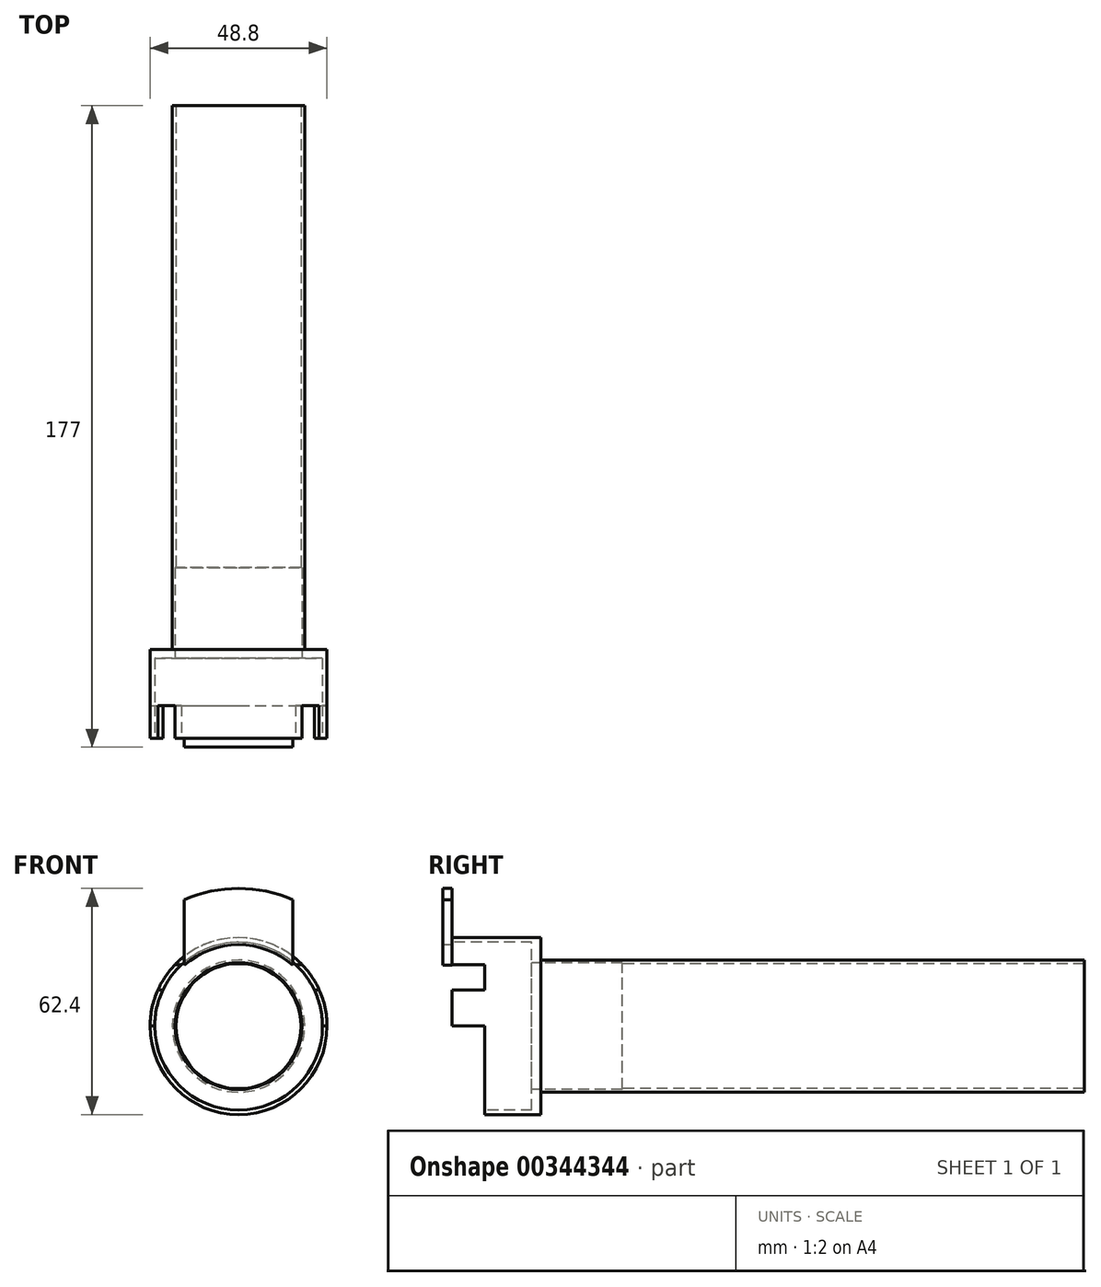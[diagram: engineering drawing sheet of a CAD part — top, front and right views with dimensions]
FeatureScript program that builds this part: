
annotation { "Feature Type Name" : "Feature", "Feature Type Description" : "" }
export const myFeature = defineFeature(function(context is Context, id is Id, definition is map)
    precondition{}
    {
        {
            var Q0;
            Q0=qCreatedBy(makeId("Front.planeOp"),FACE);
            var sketch = newSketch(context, id + "F0", { "sketchPlane" : qUnion([Q0])});
            skCircle(sketch, "E0", {"center": v(0, 0) * mm, "radius": 24.4 * mm});
            skCircle(sketch, "E1", {"center": v(0, 0) * mm, "radius": 23.15 * mm});
            skCircle(sketch, "E2", {"center": v(0, 0) * mm, "radius": 38 * mm});
            skSolve(sketch);
        }
        {
            var Q0;
            Q0=makeQuery(id+"F0.imprint","IMPRINT",FACE,{"disambiguationData":[TD([[makeQuery(id+"F0.imprint","IMPRINT",EDGE,{"derivedFrom":sQuery(id+"F0.wireOp",EDGE,"E0")}),1.0]])]});
            extrude(context, id + "F1", {"entities" : qUnion([Q0]), "oppositeDirection" : true, "depth" : 22 * mm});
        }
        {
            var Q0;
            Q0=qCreatedBy(makeId("Front.planeOp"),FACE);
            var sketch = newSketch(context, id + "F2", { "sketchPlane" : qUnion([Q0])});
            skCircle(sketch, "E3", {"center": v(0, 0) * mm, "radius": 38 * mm});
            skLineSegment(sketch, "E4", {"start": v(0, 58.74) * mm, "end": v(0, -55.93) * mm, "construction": true});
            skCircle(sketch, "E5", {"center": v(0, 0) * mm, "radius": 22.5 * mm});
            skLineSegment(sketch, "E6", {"start": v(15, 34.91) * mm, "end": v(15, 16.77) * mm});
            skLineSegment(sketch, "E7.MirrorCS", {"start": v(-15, 34.91) * mm, "end": v(-15, 16.77) * mm});
            skSolve(sketch);
        }
        {
            var Q0;
            {var subQ0=sQuery(id+"F2.wireOp",EDGE,"E6");Q0=makeQuery(id+"F2.imprint","IMPRINT",FACE,{"disambiguationData":[TD([[makeQuery(id+"F2.imprint","IMPRINT",EDGE,{"derivedFrom":subQ0}),-1.0]])]});}
            extrude(context, id + "F3", {"entities" : qUnion([Q0]), "operationType" : NewBodyOperationType.ADD, "depth" : 2.5 * mm});
        }
        {
            var Q0;
            Q0=qCreatedBy(makeId("Right.planeOp"),FACE);
            var sketch = newSketch(context, id + "F4", { "sketchPlane" : qUnion([Q0])});
            skLineSegment(sketch, "E8", {"start": v(-18.43, 0) * mm, "end": v(65.43, 0) * mm, "construction": true});
            skLineSegment(sketch, "E9", {"start": v(-16.5, 10) * mm, "end": v(49.46, 10) * mm, "construction": true});
            skLineSegment(sketch, "E10.bottom", {"start": v(0, 17) * mm, "end": v(9, 17) * mm});
            skLineSegment(sketch, "E10.top", {"start": v(0, 10) * mm, "end": v(9, 10) * mm});
            skLineSegment(sketch, "E10.left", {"start": v(0, 17) * mm, "end": v(0, 10) * mm});
            skLineSegment(sketch, "E10.right", {"start": v(9, 17) * mm, "end": v(9, 10) * mm});
            skSolve(sketch);
        }
        {
            var Q0;
            Q0 = qSketchRegion(id + "F4", true);
            extrude(context, id + "F5", {"entities" : qUnion([Q0]), "operationType" : NewBodyOperationType.REMOVE, "oppositeDirection" : true, "depth" : 25 * mm});
        }
        {
            var Q0;
            Q0=qCreatedBy(makeId("Right.planeOp"),FACE);
            var sketch = newSketch(context, id + "F6", { "sketchPlane" : qUnion([Q0])});
            skLineSegment(sketch, "E11", {"start": v(-14.75, 0) * mm, "end": v(60.77, 0) * mm, "construction": true});
            skLineSegment(sketch, "E12", {"start": v(-15.2, 10) * mm, "end": v(55.33, 10) * mm, "construction": true});
            skLineSegment(sketch, "E13.bottom", {"start": v(0, 17) * mm, "end": v(9, 17) * mm});
            skLineSegment(sketch, "E13.top", {"start": v(0, 10) * mm, "end": v(9, 10) * mm});
            skLineSegment(sketch, "E13.left", {"start": v(0, 17) * mm, "end": v(0, 10) * mm});
            skLineSegment(sketch, "E13.right", {"start": v(9, 17) * mm, "end": v(9, 10) * mm});
            skSolve(sketch);
        }
        {
            var Q0;
            Q0 = qSketchRegion(id + "F6", true);
            extrude(context, id + "F7", {"entities" : qUnion([Q0]), "operationType" : NewBodyOperationType.REMOVE, "depth" : 25 * mm});
        }
        {
            var Q0;
            Q0=qCreatedBy(makeId("Right.planeOp"),FACE);
            var sketch = newSketch(context, id + "F8", { "sketchPlane" : qUnion([Q0])});
            skLineSegment(sketch, "E14.bottom", {"start": v(0, 0) * mm, "end": v(9, 0) * mm});
            skLineSegment(sketch, "E14.top", {"start": v(0, -24.4) * mm, "end": v(9, -24.4) * mm});
            skLineSegment(sketch, "E14.left", {"start": v(0, 0) * mm, "end": v(0, -24.4) * mm});
            skLineSegment(sketch, "E14.right", {"start": v(9, 0) * mm, "end": v(9, -24.4) * mm});
            skSolve(sketch);
        }
        {
            var Q0;
            Q0 = qSketchRegion(id + "F8", true);
            extrude(context, id + "F9", {"entities" : qUnion([Q0]), "operationType" : NewBodyOperationType.REMOVE, "oppositeDirection" : true, "depth" : 25 * mm});
        }
        {
            var Q0;
            Q0=qCreatedBy(makeId("Right.planeOp"),FACE);
            var sketch = newSketch(context, id + "F10", { "sketchPlane" : qUnion([Q0])});
            skLineSegment(sketch, "E15.bottom", {"start": v(0, 0) * mm, "end": v(9, 0) * mm});
            skLineSegment(sketch, "E15.top", {"start": v(0, -24.4) * mm, "end": v(9, -24.4) * mm});
            skLineSegment(sketch, "E15.left", {"start": v(0, 0) * mm, "end": v(0, -24.4) * mm});
            skLineSegment(sketch, "E15.right", {"start": v(9, 0) * mm, "end": v(9, -24.4) * mm});
            skSolve(sketch);
        }
        {
            var Q0;
            Q0 = qSketchRegion(id + "F10", true);
            extrude(context, id + "F11", {"entities" : qUnion([Q0]), "operationType" : NewBodyOperationType.REMOVE, "depth" : 25 * mm});
        }
        {
            var Q0;
            Q0=makeQuery(id+"F1.opExtrude","CAP_FACE",FACE,{"disambiguationData":[OSD([sQuery(id+"F0.wireOp",EDGE,"E0"),sQuery(id+"F0.wireOp",EDGE,"E1")])],"isStart":false});
            var sketch = newSketch(context, id + "F12", { "sketchPlane" : qUnion([Q0])});
            skCircle(sketch, "E16", {"center": v(0, 0) * mm, "radius": 24.4 * mm});
            skSolve(sketch);
        }
        {
            var Q0;
            Q0=makeQuery(id+"F12.imprint","IMPRINT",FACE,{"disambiguationData":[TD([[makeQuery(id+"F12.imprint","IMPRINT",EDGE,{"derivedFrom":sQuery(id+"F12.wireOp",EDGE,"E16")}),-1.0]])]});
            var sketch = newSketch(context, id + "F13", { "sketchPlane" : qUnion([Q0])});
            skCircle(sketch, "E17", {"center": v(0, 0) * mm, "radius": 24.4 * mm});
            skSolve(sketch);
        }
        {
            var Q0;
            Q0 = qSketchRegion(id + "F13", true);
            var Q1;
            Q1=makeQuery(id+"F12.imprint","IMPRINT",FACE,{"disambiguationData":[TD([[makeQuery(id+"F12.imprint","IMPRINT",EDGE,{"derivedFrom":makeQuery(id+"F1.opExtrude","CAP_EDGE",EDGE,{"disambiguationData":[OSD([sQuery(id+"F0.wireOp",EDGE,"E1")])],"isStart":false})}),-1.0]])]});
            extrude(context, id + "F14", {"entities" : qUnion([Q0, Q1]), "operationType" : NewBodyOperationType.ADD, "depth" : 2.5 * mm});
        }
        {
            var Q0;
            Q0=makeQuery(id+"F14.boolean.opBoolean","MERGE",FACE,{"derivedFrom":[makeQuery(id+"F14.opExtrude","CAP_FACE",FACE,{"disambiguationData":[OSD([sQuery(id+"F0.wireOp",EDGE,"E1")])],"isStart":false}),makeQuery(id+"F14.opExtrude","CAP_FACE",FACE,{"disambiguationData":[OSD([sQuery(id+"F13.wireOp",EDGE,"E17")])],"isStart":false})]});
            var sketch = newSketch(context, id + "F15", { "sketchPlane" : qUnion([Q0])});
            skCircle(sketch, "E18", {"center": v(0, 0) * mm, "radius": 18.25 * mm});
            skCircle(sketch, "E19", {"center": v(0, 0) * mm, "radius": 17.25 * mm});
            skSolve(sketch);
        }
        {
            var Q0;
            Q0=makeQuery(id+"F15.imprint","IMPRINT",FACE,{"disambiguationData":[TD([[makeQuery(id+"F15.imprint","IMPRINT",EDGE,{"derivedFrom":sQuery(id+"F15.wireOp",EDGE,"E18")}),1.0]])]});
            extrude(context, id + "F16", {"entities" : qUnion([Q0]), "operationType" : NewBodyOperationType.ADD, "depth" : 150 * mm});
        }
        {
            var Q0;
            Q0=makeQuery(id+"F14.boolean.opBoolean","MERGE",FACE,{"derivedFrom":[makeQuery(id+"F14.opExtrude","CAP_FACE",FACE,{"disambiguationData":[OSD([sQuery(id+"F0.wireOp",EDGE,"E1")])],"isStart":true}),makeQuery(id+"F14.opExtrude","CAP_FACE",FACE,{"disambiguationData":[OSD([sQuery(id+"F13.wireOp",EDGE,"E17")])],"isStart":true})]});
            var sketch = newSketch(context, id + "F17", { "sketchPlane" : qUnion([Q0])});
            skCircle(sketch, "E20", {"center": v(0, 0) * mm, "radius": 17.5 * mm});
            skSolve(sketch);
        }
        {
            var Q0;
            Q0=makeQuery(id+"F17.imprint","IMPRINT",FACE,{"disambiguationData":[TD([[makeQuery(id+"F17.imprint","IMPRINT",EDGE,{"derivedFrom":sQuery(id+"F17.wireOp",EDGE,"E20")}),1.0]])]});
            extrude(context, id + "F18", {"entities" : qUnion([Q0]), "operationType" : NewBodyOperationType.REMOVE, "oppositeDirection" : true, "depth" : 25 * mm});
        }
    });
